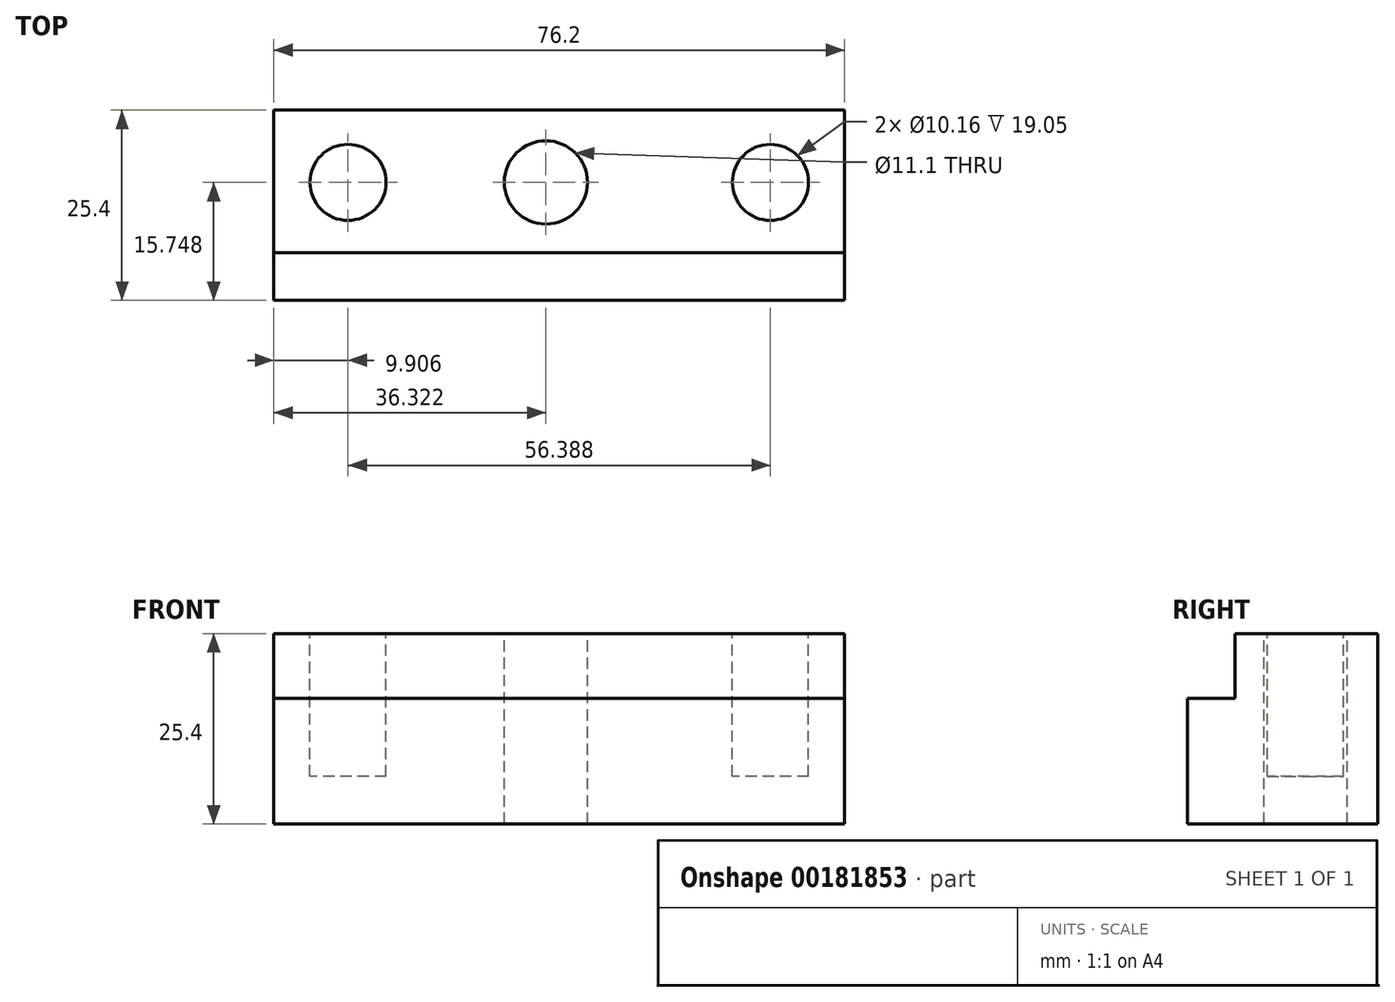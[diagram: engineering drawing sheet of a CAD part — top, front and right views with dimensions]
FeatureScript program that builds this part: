
annotation { "Feature Type Name" : "Feature", "Feature Type Description" : "" }
export const myFeature = defineFeature(function(context is Context, id is Id, definition is map)
    precondition{}
    {
        {
            var Q0;
            Q0=qCreatedBy(makeId("Right.planeOp"),FACE);
            var sketch = newSketch(context, id + "F0", { "sketchPlane" : qUnion([Q0])});
            skLineSegment(sketch, "E0.bottom", {"start": v(-12.7, 12.7) * mm, "end": v(12.7, 12.7) * mm});
            skLineSegment(sketch, "E0.top", {"start": v(-12.7, -12.7) * mm, "end": v(12.7, -12.7) * mm});
            skLineSegment(sketch, "E0.left", {"start": v(-12.7, 12.7) * mm, "end": v(-12.7, -12.7) * mm});
            skLineSegment(sketch, "E0.right", {"start": v(12.7, 12.7) * mm, "end": v(12.7, -12.7) * mm});
            skPoint(sketch, "E0.middle", {"position": v(0, 0) * mm});
            skSolve(sketch);
        }
        {
            var Q0;
            Q0 = qSketchRegion(id + "F0", true);
            extrude(context, id + "F1", {"entities" : qUnion([Q0]), "oppositeDirection" : true, "depth" : 76.2 * mm});
        }
        {
            var Q0;
            Q0=qCreatedBy(makeId("Right.planeOp"),FACE);
            var sketch = newSketch(context, id + "F2", { "sketchPlane" : qUnion([Q0])});
            skLineSegment(sketch, "E1.bottom", {"start": v(-12.7, 4.06) * mm, "end": v(-6.35, 4.06) * mm});
            skLineSegment(sketch, "E1.top", {"start": v(-12.7, 12.7) * mm, "end": v(-6.35, 12.7) * mm});
            skLineSegment(sketch, "E1.left", {"start": v(-12.7, 4.06) * mm, "end": v(-12.7, 12.7) * mm});
            skLineSegment(sketch, "E1.right", {"start": v(-6.35, 4.06) * mm, "end": v(-6.35, 12.7) * mm});
            skSolve(sketch);
        }
        {
            var Q0;
            Q0 = qSketchRegion(id + "F2", true);
            extrude(context, id + "F3", {"entities" : qUnion([Q0]), "operationType" : NewBodyOperationType.REMOVE, "oppositeDirection" : true, "depth" : 76.2 * mm});
        }
        {
            var Q0;
            Q0=makeQuery(id+"F1.opExtrude","SWEPT_FACE",FACE,{"disambiguationData":[OSD([sQuery(id+"F0.wireOp",EDGE,"E0.bottom")])]});
            var sketch = newSketch(context, id + "F4", { "sketchPlane" : qUnion([Q0])});
            skCircle(sketch, "E2", {"center": v(-66.3, 3.05) * mm, "radius": 5.08 * mm});
            skCircle(sketch, "E3", {"center": v(-9.9, 3.05) * mm, "radius": 5.08 * mm});
            skSolve(sketch);
        }
        {
            var Q0;
            Q0 = qSketchRegion(id + "F4", true);
            extrude(context, id + "F5", {"entities" : qUnion([Q0]), "operationType" : NewBodyOperationType.REMOVE, "oppositeDirection" : true, "depth" : 19.05 * mm});
        }
        {
            var Q0;
            Q0=makeQuery(id+"F1.opExtrude","SWEPT_FACE",FACE,{"disambiguationData":[OSD([sQuery(id+"F0.wireOp",EDGE,"E0.bottom")])]});
            var sketch = newSketch(context, id + "F6", { "sketchPlane" : qUnion([Q0])});
            skCircle(sketch, "E4", {"center": v(-39.88, 3.05) * mm, "radius": 5.55 * mm});
            skSolve(sketch);
        }
        {
            var Q0;
            Q0 = qSketchRegion(id + "F6", true);
            extrude(context, id + "F7", {"entities" : qUnion([Q0]), "operationType" : NewBodyOperationType.REMOVE, "oppositeDirection" : true, "depth" : 73.4 * mm});
        }
    });
